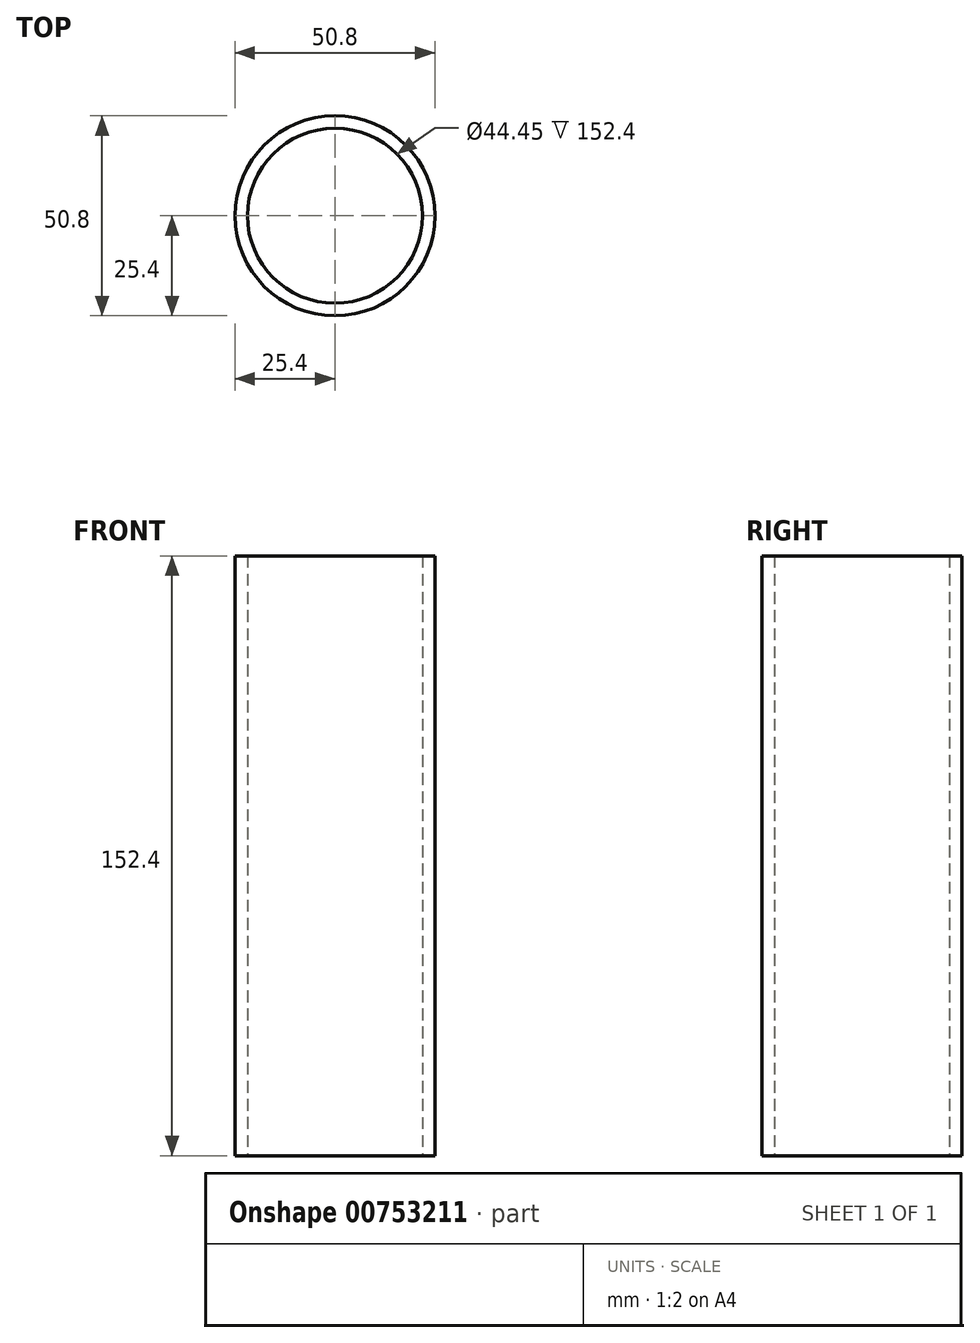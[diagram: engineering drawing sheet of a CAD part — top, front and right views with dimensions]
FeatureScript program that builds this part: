
annotation { "Feature Type Name" : "Feature", "Feature Type Description" : "" }
export const myFeature = defineFeature(function(context is Context, id is Id, definition is map)
    precondition{}
    {
        {
            var Q0;
            Q0=qCreatedBy(makeId("Top.planeOp"),FACE);
            var sketch = newSketch(context, id + "F0", { "sketchPlane" : qUnion([Q0])});
            skCircle(sketch, "E0", {"center": v(0, 0) * mm, "radius": 25.4 * mm});
            skCircle(sketch, "E1.0", {"center": v(0, 0) * mm, "radius": 22.23 * mm});
            skSolve(sketch);
        }
        {
            var Q0;
            Q0=makeQuery(id+"F0.imprint","IMPRINT",FACE,{"disambiguationData":[TD([[makeQuery(id+"F0.imprint","IMPRINT",EDGE,{"derivedFrom":sQuery(id+"F0.wireOp",EDGE,"E0")}),1.0]])]});
            var Q1;
            Q1=sQuery(id+"F0.wireOp",EDGE,"E1.0");
            var Q2;
            Q2=sQuery(id+"F0.wireOp",EDGE,"E0");
            extrude(context, id + "F1", {"entities" : qUnion([Q0]), "surfaceEntities" : qUnion([Q1, Q2]), "depth" : 152.4 * mm, "offsetDistance" : 25.4 * mm});
        }
    });
